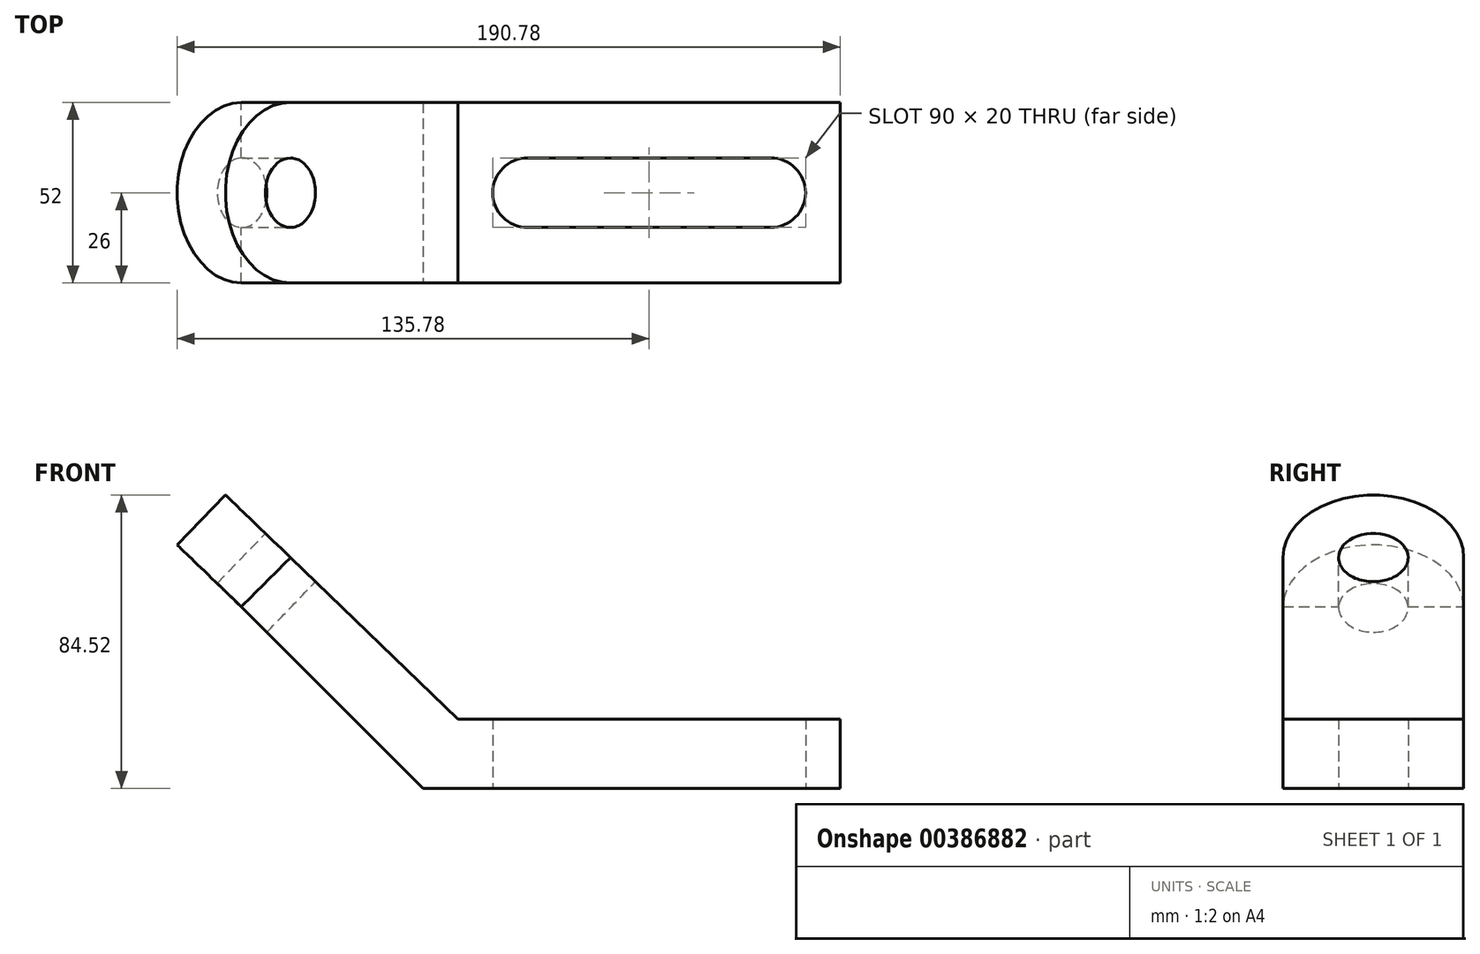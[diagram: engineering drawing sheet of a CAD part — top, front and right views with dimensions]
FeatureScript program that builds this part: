
annotation { "Feature Type Name" : "Feature", "Feature Type Description" : "" }
export const myFeature = defineFeature(function(context is Context, id is Id, definition is map)
    precondition{}
    {
        {
            var Q0;
            Q0=qCreatedBy(makeId("Top.planeOp"),FACE);
            var sketch = newSketch(context, id + "F0", { "sketchPlane" : qUnion([Q0])});
            skArc(sketch, "E0", {"start": v(20, 36) * mm, "mid": v(10, 26) * mm, "end": v(20, 16) * mm});
            skLineSegment(sketch, "E1.bottom", {"start": v(20, 36) * mm, "end": v(90, 36) * mm});
            skLineSegment(sketch, "E1.top", {"start": v(20, 16) * mm, "end": v(90, 16) * mm});
            skArc(sketch, "E2", {"start": v(90, 16) * mm, "mid": v(100, 26) * mm, "end": v(90, 36) * mm});
            skPoint(sketch, "E3.end.orphan", {"position": v(100, 26) * mm});
            skPoint(sketch, "E4.top.end.orphan", {"position": v(100, 52) * mm});
            skPoint(sketch, "E4.bottom.end.orphan", {"position": v(100, 0) * mm});
            skPoint(sketch, "E5.end.orphan", {"position": v(0, 26) * mm});
            skPoint(sketch, "E6.orphan", {"position": v(0, 0) * mm});
            skPoint(sketch, "E4.left.end.orphan", {"position": v(0, 52) * mm});
            skLineSegment(sketch, "E7.bottom", {"start": v(0, 0) * mm, "end": v(110, 0) * mm});
            skLineSegment(sketch, "E7.top", {"start": v(0, 52) * mm, "end": v(110, 52) * mm});
            skLineSegment(sketch, "E7.left", {"start": v(0, 0) * mm, "end": v(0, 52) * mm});
            skLineSegment(sketch, "E7.right", {"start": v(110, 0) * mm, "end": v(110, 52) * mm});
            skSolve(sketch);
        }
        {
            var Q0;
            Q0=makeQuery(id+"F0.imprint","IMPRINT",FACE,{"disambiguationData":[TD([[makeQuery(id+"F0.imprint","IMPRINT",EDGE,{"derivedFrom":sQuery(id+"F0.wireOp",EDGE,"E0")}),-1.0]])]});
            extrude(context, id + "F1", {"entities" : qUnion([Q0]), "depth" : 20 * mm});
        }
        {
            var Q0;
            Q0=makeQuery(id+"F1.opExtrude","SWEPT_FACE",FACE,{"disambiguationData":[OSD([sQuery(id+"F0.wireOp",EDGE,"E7.bottom")])]});
            var sketch = newSketch(context, id + "F2", { "sketchPlane" : qUnion([Q0])});
            skLineSegment(sketch, "E8", {"start": v(0, 0) * mm, "end": v(-10, 0) * mm});
            skLineSegment(sketch, "E9", {"start": v(-10, 0) * mm, "end": v(0, 20) * mm});
            skSolve(sketch);
        }
        {
            var Q0;
            Q0=makeQuery(id+"F2.imprint","IMPRINT",FACE,{"disambiguationData":[TD([[makeQuery(id+"F2.imprint","IMPRINT",EDGE,{"derivedFrom":sQuery(id+"F2.wireOp",EDGE,"E8")}),-1.0]])]});
            extrude(context, id + "F3", {"entities" : qUnion([Q0]), "operationType" : NewBodyOperationType.ADD, "oppositeDirection" : true, "depth" : 52 * mm});
        }
        {
            var Q0;
            {var subQ0=sQuery(id+"F0.wireOp",EDGE,"E7.bottom");Q0=makeQuery(id+"F3.boolean.opBoolean","MERGE",FACE,{"derivedFrom":[makeQuery(id+"F1.opExtrude","SWEPT_FACE",FACE,{"disambiguationData":[OSD([subQ0])]}),makeQuery(id+"F3.opExtrude","CAP_FACE",FACE,{"disambiguationData":[OSD([subQ0,sQuery(id+"F0.wireOp",EDGE,"E7.left"),sQuery(id+"F2.wireOp",EDGE,"E8"),sQuery(id+"F2.wireOp",EDGE,"E9")])],"isStart":true})]});}
            var sketch = newSketch(context, id + "F4", { "sketchPlane" : qUnion([Q0])});
            skLineSegment(sketch, "E10", {"start": v(-10, 0) * mm, "end": v(-62.33, 52.33) * mm});
            skLineSegment(sketch, "E11", {"start": v(-62.33, 52.33) * mm, "end": v(-48.18, 66.47) * mm});
            skLineSegment(sketch, "E12", {"start": v(-48.18, 66.47) * mm, "end": v(0, 20) * mm});
            skPoint(sketch, "E13.end.orphan", {"position": v(-46.47, 66.47) * mm});
            skSolve(sketch);
        }
        {
            var Q0;
            Q0=makeQuery(id+"F4.imprint","IMPRINT",FACE,{"disambiguationData":[TD([[makeQuery(id+"F4.imprint","IMPRINT",EDGE,{"derivedFrom":sQuery(id+"F4.wireOp",EDGE,"E10")}),-1.0]])]});
            extrude(context, id + "F5", {"entities" : qUnion([Q0]), "operationType" : NewBodyOperationType.ADD, "oppositeDirection" : true, "depth" : 52 * mm});
        }
        {
            var Q0;
            Q0=makeQuery(id+"F5.opExtrude","SWEPT_FACE",FACE,{"disambiguationData":[OSD([sQuery(id+"F4.wireOp",EDGE,"E12")])]});
            var sketch = newSketch(context, id + "F6", { "sketchPlane" : qUnion([Q0])});
            skCircle(sketch, "E14", {"center": v(-80.82, 26) * mm, "radius": 26 * mm});
            skSolve(sketch);
        }
        {
            var Q0;
            {var subQ1=sQuery(id+"F4.wireOp",EDGE,"E12");var subQ2=makeQuery(id+"F5.opExtrude","SWEPT_EDGE",EDGE,{"disambiguationData":[OSD([sQuery(id+"F4.wireOp",EDGE,"E11"),subQ1])]});Q0=makeQuery(id+"F6.imprint","IMPRINT",FACE,{"disambiguationData":[TD([[makeQuery(id+"F6.imprint","IMPRINT",EDGE,{"derivedFrom":subQ2}),-1.0]])]});}
            extrude(context, id + "F7", {"entities" : qUnion([Q0]), "operationType" : NewBodyOperationType.ADD, "oppositeDirection" : true, "depth" : 20 * mm});
        }
        {
            var Q0;
            {var subQ0=sQuery(id+"F4.wireOp",EDGE,"E12");Q0=makeQuery(id+"F7.boolean.opBoolean","MERGE",FACE,{"derivedFrom":[makeQuery(id+"F5.opExtrude","SWEPT_FACE",FACE,{"disambiguationData":[OSD([subQ0])]}),makeQuery(id+"F7.opExtrude","CAP_FACE",FACE,{"disambiguationData":[OSD([sQuery(id+"F4.wireOp",EDGE,"E11"),subQ0,sQuery(id+"F6.wireOp",EDGE,"E14")])],"isStart":true})]});}
            var sketch = newSketch(context, id + "F8", { "sketchPlane" : qUnion([Q0])});
            skLineSegment(sketch, "E15", {"start": v(-80.82, 0) * mm, "end": v(-80.82, 26) * mm});
            skCircle(sketch, "E16", {"center": v(-80.82, 26) * mm, "radius": 10 * mm});
            skSolve(sketch);
        }
        {
            var Q0;
            Q0=makeQuery(id+"F8.imprint","IMPRINT",FACE,{"disambiguationData":[TD([[makeQuery(id+"F8.imprint","IMPRINT",EDGE,{"derivedFrom":sQuery(id+"F8.wireOp",EDGE,"E16")}),1.0]])]});
            extrude(context, id + "F9", {"entities" : qUnion([Q0]), "operationType" : NewBodyOperationType.REMOVE, "endBound" : BoundingType.THROUGH_ALL, "oppositeDirection" : true, "depth" : 25 * mm});
        }
    });
